FCSTD DOCUMENT  (FreeCAD 0.20R29603 (Git))
Label: frontpanel_with_guides - Copy (2)
License: All rights reserved
LicenseURL: http://en.wikipedia.org/wiki/All_rights_reserved
objects: App::TextDocument×1, Sketcher::SketchObject×1
note: 1 computed .brp shape members not serialized (recipe doc carries the construction recipe); baked Part::Feature solids carry a one-line shape summary decoded from their .brp

FEATURE [App::TextDocument] Text_document  label="Text document"
FEATURE [Sketcher::SketchObject] Sketch
  FullyConstrained = false
  sketch-geometry (27):
    g0: LineSegment StartX=0 StartY=2.84e-14 StartZ=0 EndX=426 EndY=2.84e-14 EndZ=0
    g1: LineSegment StartX=426 StartY=2.84e-14 StartZ=0 EndX=426 EndY=90 EndZ=0
    g2: LineSegment StartX=426 StartY=90 StartZ=0 EndX=0 EndY=90 EndZ=0
    g3: LineSegment StartX=0 StartY=90 StartZ=0 EndX=0 EndY=2.84e-14 EndZ=0
    g4: LineSegment StartX=136 StartY=45 StartZ=0 EndX=136 EndY=85 EndZ=0
    g5: LineSegment StartX=136 StartY=85 StartZ=0 EndX=40 EndY=85 EndZ=0
    g6: LineSegment StartX=40 StartY=85 StartZ=0 EndX=40 EndY=45 EndZ=0
    g7: LineSegment StartX=0 StartY=2.84e-14 StartZ=0 EndX=40 EndY=0 EndZ=0
    g8: LineSegment StartX=406.073 StartY=30 StartZ=0 EndX=415.98 EndY=30 EndZ=0
    g9: LineSegment StartX=415.98 StartY=30 StartZ=0 EndX=415.98 EndY=60 EndZ=0
    g10: LineSegment StartX=415.98 StartY=60 StartZ=0 EndX=406.073 EndY=60 EndZ=0
    g11: LineSegment StartX=406.073 StartY=60 StartZ=0 EndX=406.073 EndY=30 EndZ=0
    g12: Circle CenterX=40 CenterY=23 CenterZ=0 NormalX=0 NormalY=0 NormalZ=1 AngleXU=0 Radius=5
    g13: Circle CenterX=70 CenterY=23 CenterZ=0 NormalX=0 NormalY=0 NormalZ=1 AngleXU=0 Radius=4
    g14: Circle CenterX=245 CenterY=23 CenterZ=0 NormalX=0 NormalY=0 NormalZ=1 AngleXU=0 Radius=3
    g15: Circle CenterX=110 CenterY=23 CenterZ=0 NormalX=0 NormalY=0 NormalZ=1 AngleXU=0 Radius=3
    g16: Circle CenterX=130 CenterY=23 CenterZ=0 NormalX=0 NormalY=0 NormalZ=1 AngleXU=0 Radius=3
    g17: Circle CenterX=225 CenterY=23 CenterZ=0 NormalX=0 NormalY=0 NormalZ=1 AngleXU=0 Radius=2.54933
    g18: Circle CenterX=265 CenterY=23 CenterZ=0 NormalX=0 NormalY=0 NormalZ=1 AngleXU=0 Radius=2.53523
    g19: Circle CenterX=175 CenterY=23 CenterZ=0 NormalX=0 NormalY=0 NormalZ=1 AngleXU=0 Radius=4
    g20: Circle CenterX=225 CenterY=67 CenterZ=0 NormalX=0 NormalY=0 NormalZ=1 AngleXU=0 Radius=4.50244
    g21: Circle CenterX=275 CenterY=67 CenterZ=0 NormalX=0 NormalY=0 NormalZ=1 AngleXU=0 Radius=4.5408
    g22: Circle CenterX=175 CenterY=67 CenterZ=0 NormalX=0 NormalY=0 NormalZ=1 AngleXU=0 Radius=4.48593
    g23: Circle CenterX=325 CenterY=67 CenterZ=0 NormalX=0 NormalY=0 NormalZ=1 AngleXU=0 Radius=4.53603
    g24: Circle CenterX=366 CenterY=45 CenterZ=0 NormalX=0 NormalY=0 NormalZ=1 AngleXU=0 Radius=4
    g25: Circle CenterX=411 CenterY=76 CenterZ=0 NormalX=0 NormalY=0 NormalZ=1 AngleXU=0 Radius=2.48663
    g26: LineSegment StartX=40 StartY=45 StartZ=0 EndX=136 EndY=45 EndZ=0
  constraints (40):
    c: Coincident(g0,g1)
    c: Coincident(g1,g2)
    c: Coincident(g2,g3)
    c: Coincident(g3,g0)
    c: Horizontal(g0)
    c: Horizontal(g2)
    c: Vertical(g1)
    c: Vertical(g3)
    c: Coincident(g4,g5)
    c: Coincident(g5,g6)
    c: Horizontal(g5)
    c: Vertical(g4)
    c: Vertical(g6)
    c: DistanceX(g0,g0) = 426
    c: DistanceY(g0,g2) = 90
    c: DistanceY(g6,g5) = 40
    c: DistanceX(g5,g4) = 96
    c: Coincident(g7,g0)
    c: Coincident(g8,g9)
    c: Coincident(g9,g10)
    c: Coincident(g10,g11)
    c: Coincident(g11,g8)
    c: Horizontal(g8)
    c: Horizontal(g10)
    c: Vertical(g9)
    c: Vertical(g11)
    c: DistanceX(g12,g13) = 30
    c: DistanceX(g13,g15) = 40
    c: DistanceX(g15,g16) = 20
    c: DistanceX(g16,g19) = 45
    c: DistanceX(g19,g17) = 50
    c: DistanceX(g17,g14) = 20
    c: DistanceX(g14,g18) = 20
    c: DistanceX(g22,g20) = 50
    c: DistanceX(g20,g21) = 50
    c: DistanceX(g21,g23) = 50
    c: DistanceX(g0,g-1) = 0
    c: Coincident(g26,g6)
    c: Coincident(g26,g4)
    c: Horizontal(g26)
